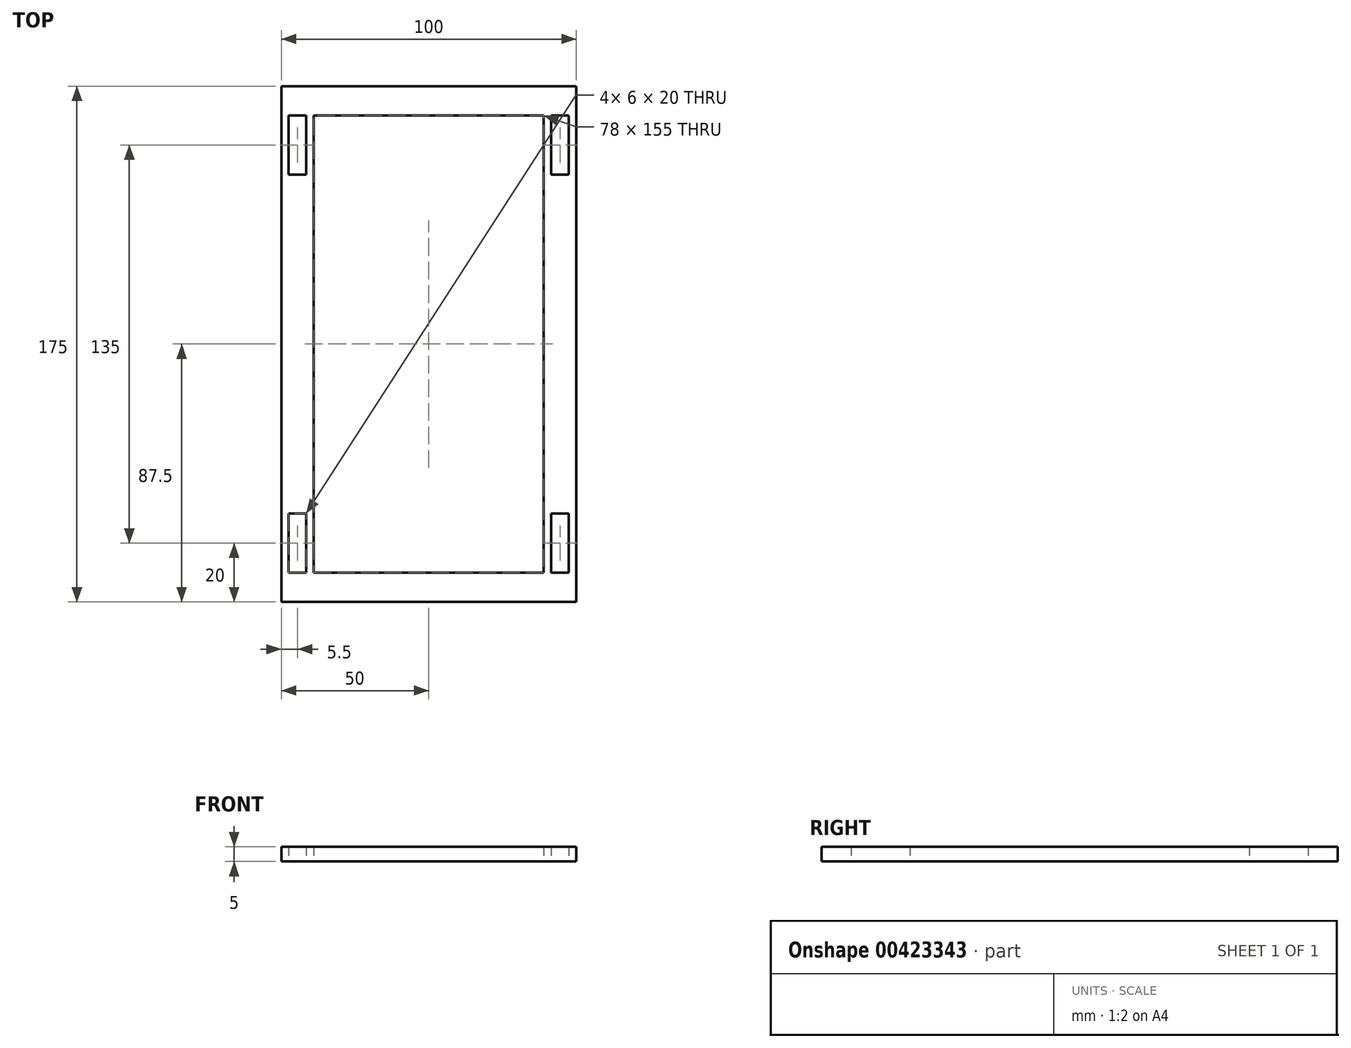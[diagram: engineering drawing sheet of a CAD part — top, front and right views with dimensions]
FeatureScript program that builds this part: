
annotation { "Feature Type Name" : "Feature", "Feature Type Description" : "" }
export const myFeature = defineFeature(function(context is Context, id is Id, definition is map)
    precondition{}
    {
        {
            var Q0;
            Q0=qCreatedBy(makeId("Top.planeOp"),FACE);
            var sketch = newSketch(context, id + "F0", { "sketchPlane" : qUnion([Q0])});
            skLineSegment(sketch, "E0.bottom", {"start": v(50, 87.5) * mm, "end": v(-50, 87.5) * mm});
            skLineSegment(sketch, "E0.top", {"start": v(50, -87.5) * mm, "end": v(-50, -87.5) * mm});
            skLineSegment(sketch, "E0.left", {"start": v(50, 87.5) * mm, "end": v(50, -87.5) * mm});
            skLineSegment(sketch, "E0.right", {"start": v(-50, 87.5) * mm, "end": v(-50, -87.5) * mm});
            skPoint(sketch, "E0.middle", {"position": v(0, 0) * mm});
            skLineSegment(sketch, "E1.bottom", {"start": v(-41.5, -57.5) * mm, "end": v(-47.5, -57.5) * mm});
            skLineSegment(sketch, "E1.top", {"start": v(-41.5, -77.5) * mm, "end": v(-47.5, -77.5) * mm});
            skLineSegment(sketch, "E1.left", {"start": v(-41.5, -57.5) * mm, "end": v(-41.5, -77.5) * mm});
            skLineSegment(sketch, "E1.right", {"start": v(-47.5, -57.5) * mm, "end": v(-47.5, -77.5) * mm});
            skPoint(sketch, "E1.middle", {"position": v(-44.5, -67.5) * mm});
            skLineSegment(sketch, "E2.MirrorCS", {"start": v(41.5, -57.5) * mm, "end": v(41.5, -77.5) * mm});
            skLineSegment(sketch, "E3.MirrorCS", {"start": v(41.5, -57.5) * mm, "end": v(47.5, -57.5) * mm});
            skLineSegment(sketch, "E4.MirrorCS", {"start": v(47.5, -57.5) * mm, "end": v(47.5, -77.5) * mm});
            skLineSegment(sketch, "E5.MirrorCS", {"start": v(41.5, -77.5) * mm, "end": v(47.5, -77.5) * mm});
            skLineSegment(sketch, "E6.bottom", {"start": v(-41.5, 77.5) * mm, "end": v(-47.5, 77.5) * mm});
            skLineSegment(sketch, "E6.top", {"start": v(-41.5, 57.5) * mm, "end": v(-47.5, 57.5) * mm});
            skLineSegment(sketch, "E6.left", {"start": v(-41.5, 77.5) * mm, "end": v(-41.5, 57.5) * mm});
            skLineSegment(sketch, "E6.right", {"start": v(-47.5, 77.5) * mm, "end": v(-47.5, 57.5) * mm});
            skPoint(sketch, "E6.middle", {"position": v(-44.5, 67.5) * mm});
            skLineSegment(sketch, "E7.MirrorCS", {"start": v(41.5, 77.5) * mm, "end": v(47.5, 77.5) * mm});
            skLineSegment(sketch, "E8.MirrorCS", {"start": v(41.5, 77.5) * mm, "end": v(41.5, 57.5) * mm});
            skLineSegment(sketch, "E9.MirrorCS", {"start": v(47.5, 77.5) * mm, "end": v(47.5, 57.5) * mm});
            skLineSegment(sketch, "E10.MirrorCS", {"start": v(41.5, 57.5) * mm, "end": v(47.5, 57.5) * mm});
            skLineSegment(sketch, "E11.bottom", {"start": v(-39, 77.5) * mm, "end": v(39, 77.5) * mm});
            skLineSegment(sketch, "E11.top", {"start": v(-39, -77.5) * mm, "end": v(39, -77.5) * mm});
            skLineSegment(sketch, "E11.left", {"start": v(-39, 77.5) * mm, "end": v(-39, -77.5) * mm});
            skLineSegment(sketch, "E11.right", {"start": v(39, 77.5) * mm, "end": v(39, -77.5) * mm});
            skSolve(sketch);
        }
        {
            var Q0;
            Q0=makeQuery(id+"F0.imprint","IMPRINT",FACE,{"disambiguationData":[TD([[makeQuery(id+"F0.imprint","IMPRINT",EDGE,{"derivedFrom":sQuery(id+"F0.wireOp",EDGE,"E0.bottom")}),1.0]])]});
            extrude(context, id + "F1", {"entities" : qUnion([Q0]), "depth" : 5 * mm});
        }
    });
